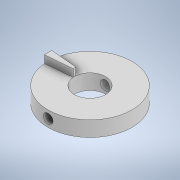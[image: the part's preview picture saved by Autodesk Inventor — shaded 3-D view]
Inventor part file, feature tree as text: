
AUTODESK INVENTOR PART (.ipt)
format: ipt  version: 2021 (Build 250183000, 183)  size: 133,632 bytes
history: native  units: mm
features: extrude x3, sketch x2
ambient origin geometry x8: Origin, YZ Plane, XZ Plane, XY Plane, X Axis, Y Axis, Z Axis, Center Point
bodies: Solid1 (feature_tree)
feature tree (5):
  extrude  "Extrusion1"  Depth=22.0mm
  extrude  "Extrusion2"  Depth=2.0mm
  extrude  "Extrusion3"  Depth=2.0mm TaperAngle=0.0deg
  sketch  "Sketch1"  dims[d0=8.2mm d1=22.0mm]
  sketch  "Sketch3"  dims[d2=4.0mm d3=0.0mm d4=1.745329mm d5=2.0mm d6=0.0mm d7=2.5mm d8=2.0mm d9=12.75mm d10=0.0mm]
